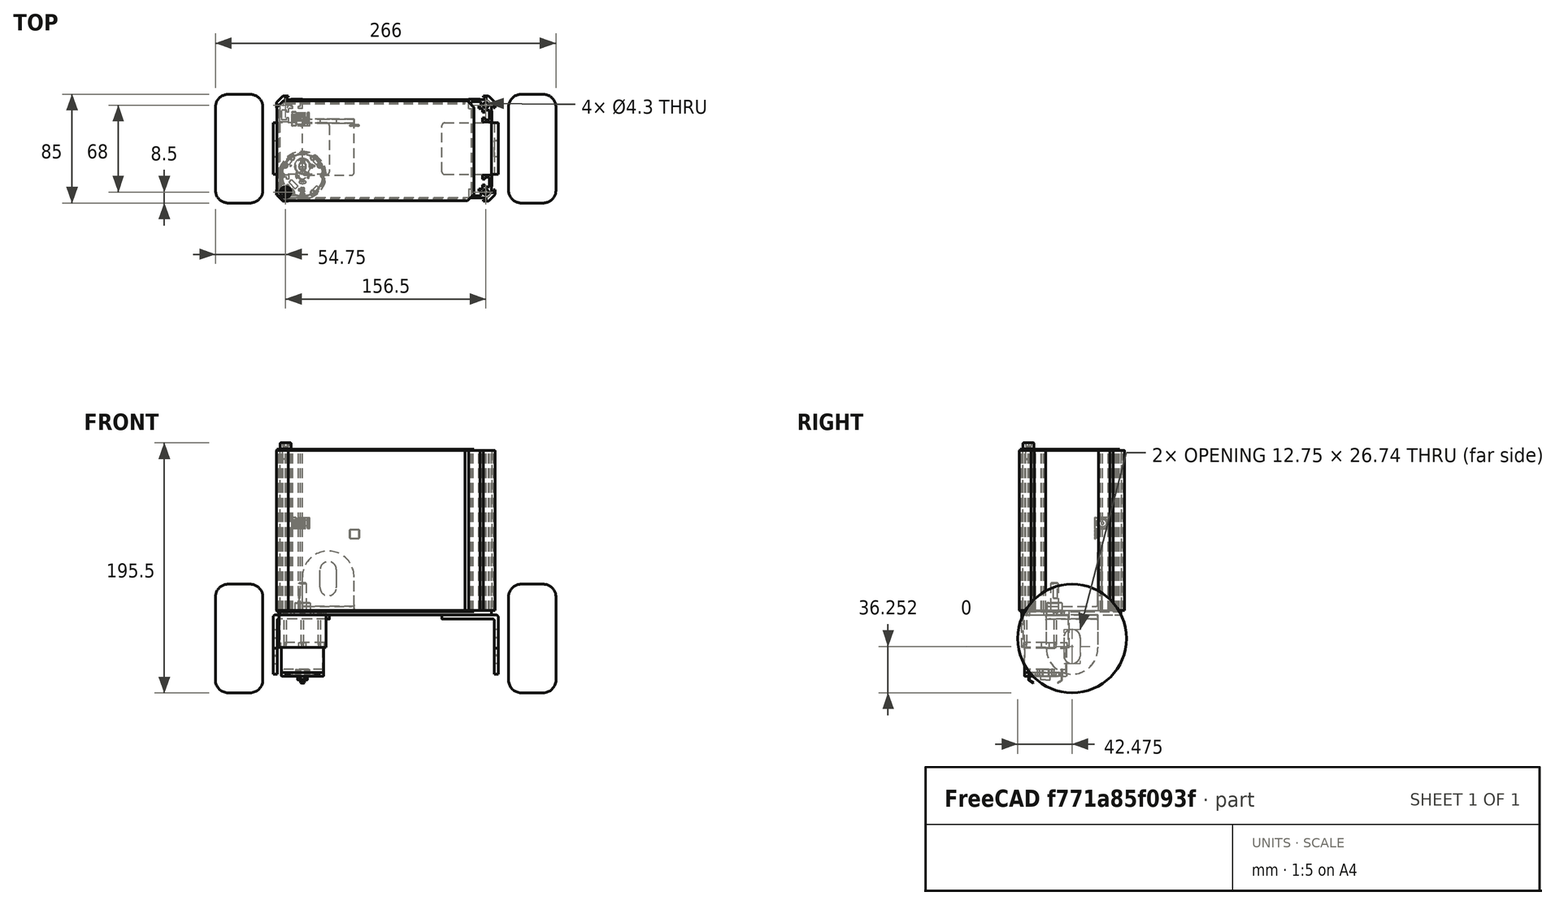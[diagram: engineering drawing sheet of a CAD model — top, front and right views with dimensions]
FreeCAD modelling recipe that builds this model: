
FCSTD DOCUMENT  (FreeCAD 0.18R16146 (Git))
Label: b1m1
License: All rights reserved
LicenseURL: http://en.wikipedia.org/wiki/All_rights_reserved
objects: Part::Feature×76, Part::Box×10, Part::Cylinder×5, App::DocumentObjectGroup×4, Part::Fillet×4, App::Part×3, Part::Cut×3, Part::Chamfer×2, Part::MultiFuse×2, Part::FeaturePython×1
note: 103 computed .brp shape members not serialized (recipe doc carries the construction recipe); baked Part::Feature solids carry a one-line shape summary decoded from their .brp

FEATURE [Part::Feature] Fillet001  label="frame_001"
  Placement = pos=(0,0,0) rot=(0,0,1;3.14159rad)
  shape: bbox 20.35 x 20.35 x 125 mm, 40 faces (baked)
FEATURE [Part::Feature] Fillet002  label="frame_002"
  Placement = pos=(130,0,0) rot=(0,0,-1;1.5708rad)
  shape: bbox 20.35 x 20.35 x 125 mm, 40 faces (baked)
FEATURE [Part::Feature] Fillet003  label="frame_003"
  Placement = pos=(0,41.5,0) rot=(0,0,1;1.5708rad)
  shape: bbox 20.35 x 20.35 x 125 mm, 40 faces (baked)
FEATURE [Part::Feature] Fillet004  label="frame_004"
  Placement = pos=(130,41.5,0) rot=(0,0,1;0rad)
  shape: bbox 20.35 x 20.35 x 125 mm, 40 faces (baked)
FEATURE [Part::Feature] Part__Feature013001  label="power jack back-002"
  shape: bbox 2 x 10.5 x 8 mm, 39 faces (baked)
FEATURE [Part::Feature] Part__Feature005001  label="10 pins-013"
  shape: bbox 0.5 x 3 x 0.5 mm, 29 faces, 0 solids (baked)
FEATURE [Part::Feature] Part__Feature027001  label="8 pin-026"
  shape: bbox 0.5 x 3 x 0.5 mm, 13 faces, 0 solids (baked)
FEATURE [Part::Feature] Part__Feature048  label="PCB"
  shape: bbox 68 x 2 x 53 mm, 960 faces, 0 solids (baked)
FEATURE [Part::Feature] Part__Feature009001  label="10 pins-018"
  shape: bbox 0.5 x 3 x 0.5 mm, 29 faces, 0 solids (baked)
FEATURE [Part::Feature] Part__Feature002001  label="10 pins-017"
  shape: bbox 0.5 x 3 x 0.5 mm, 29 faces, 0 solids (baked)
FEATURE [Part::Feature] Part__Feature021001  label="8 pin-021"
  shape: bbox 21 x 8.5 x 2.5 mm, 78 faces, 0 solids (baked)
FEATURE [Part::Feature] Part__Feature007001  label="10 pins-014"
  shape: bbox 0.5 x 3 x 0.5 mm, 29 faces, 0 solids (baked)
FEATURE [Part::Feature] Part__Feature039001  label="6 pin-012"
  shape: bbox 16 x 8.5 x 2.5 mm, 69 faces, 0 solids (baked)
FEATURE [Part::Feature] Part__Feature012001  label="power jack-002"
  shape: bbox 12 x 11 x 9 mm, 137 faces (baked)
FEATURE [Part::Feature] Part__Feature023001  label="8 pin-025"
  shape: bbox 0.5 x 3 x 0.5 mm, 13 faces, 0 solids (baked)
FEATURE [Part::Feature] Part__Feature037001  label="8 pin-018"
  shape: bbox 0.5 x 3 x 0.5 mm, 13 faces, 0 solids (baked)
FEATURE [Part::Feature] Part__Feature038001  label="8 pin-022"
  shape: bbox 0.5 x 3 x 0.5 mm, 13 faces, 0 solids (baked)
FEATURE [Part::Feature] Part__Feature018001  label="pin 2-008"
  shape: bbox 5 x 10 x 2 mm, 34 faces, 0 solids (baked)
FEATURE [Part::Feature] Part__Feature031001  label="8 pin-027"
  shape: bbox 0.5 x 3 x 0.5 mm, 13 faces, 0 solids (baked)
FEATURE [Part::Feature] Part__Feature014001  label="power jack pin-002"
  shape: bbox 12.6 x 11.32 x 4 mm, 660 faces, 0 solids (baked)
FEATURE [Part::Feature] Part__Feature045001  label="6 pin-010"
  shape: bbox 0.5 x 3 x 0.5 mm, 13 faces, 0 solids (baked)
FEATURE [Part::Feature] Part__Feature032001  label="8 pin-029"
  shape: bbox 0.5 x 3 x 0.5 mm, 13 faces, 0 solids (baked)
FEATURE [Part::Feature] Part__Feature010001  label="10 pins-021"
  shape: bbox 0.5 x 3 x 0.5 mm, 29 faces, 0 solids (baked)
FEATURE [Part::Feature] Part__Feature026001  label="8 pin-032"
  shape: bbox 0.5 x 3 x 0.5 mm, 13 faces, 0 solids (baked)
FEATURE [Part::Feature] Part__Feature040001  label="6 pin-014"
  shape: bbox 0.5 x 3 x 0.5 mm, 13 faces, 0 solids (baked)
FEATURE [Part::Feature] Part__Feature008001  label="10 pins-020"
  shape: bbox 0.5 x 3 x 0.5 mm, 29 faces, 0 solids (baked)
FEATURE [Part::Feature] Part__Feature020001  label="chip-002"
  shape: bbox 7.6 x 1 x 7.6 mm, 182 faces (baked)
FEATURE [Part::Feature] Part__Feature004001  label="10 pins-012"
  shape: bbox 0.5 x 3 x 0.5 mm, 29 faces, 0 solids (baked)
FEATURE [Part::Feature] Part__Feature001001  label="10 pins-019"
  shape: bbox 26 x 8.5 x 2.5 mm, 96 faces, 0 solids (baked)
FEATURE [Part::Feature] Part__Feature036001  label="8 pin-023"
  shape: bbox 0.5 x 3 x 0.5 mm, 13 faces, 0 solids (baked)
FEATURE [Part::Feature] Part__Feature022001  label="8 pin-034"
  shape: bbox 0.5 x 3 x 0.5 mm, 13 faces, 0 solids (baked)
FEATURE [Part::Feature] Part__Feature043001  label="6 pin-015"
  shape: bbox 0.5 x 3 x 0.5 mm, 13 faces, 0 solids (baked)
FEATURE [Part::Feature] Part__Feature042001  label="6 pin-013"
  shape: bbox 0.5 x 3 x 0.5 mm, 13 faces, 0 solids (baked)
FEATURE [Part::Feature] Part__Feature028001  label="8 pin-024"
  shape: bbox 0.5 x 3 x 0.5 mm, 13 faces, 0 solids (baked)
FEATURE [Part::Feature] Part__Feature044001  label="6 pin-016"
  shape: bbox 0.5 x 3 x 0.5 mm, 13 faces, 0 solids (baked)
FEATURE [Part::Feature] Part__Feature006001  label="10 pins-015"
  shape: bbox 0.5 x 3 x 0.5 mm, 29 faces, 0 solids (baked)
FEATURE [Part::Feature] Part__Feature015001  label="power jack pin 1-002"
  shape: bbox 8.476 x 8 x 6.5 mm, 49 faces, 0 solids (baked)
FEATURE [Part::Feature] Part__Feature029001  label="8 pin-033"
  shape: bbox 0.5 x 3 x 0.5 mm, 13 faces, 0 solids (baked)
FEATURE [Part::Feature] Part__Feature017001  label="pin 2-006"
  shape: bbox 5 x 10 x 2 mm, 34 faces, 0 solids (baked)
FEATURE [Part::Feature] Part__Feature034001  label="8 pin-030"
  shape: bbox 0.5 x 3 x 0.5 mm, 13 faces, 0 solids (baked)
FEATURE [Part::Feature] Part__Feature041001  label="6 pin-011"
  shape: bbox 0.5 x 3 x 0.5 mm, 13 faces, 0 solids (baked)
FEATURE [Part::Feature] Part__Feature030001  label="8 pin-035"
  shape: bbox 21 x 8.5 x 2.5 mm, 78 faces, 0 solids (baked)
FEATURE [Part::Feature] Part__Feature025001  label="8 pin-019"
  shape: bbox 0.5 x 3 x 0.5 mm, 13 faces, 0 solids (baked)
FEATURE [Part::Feature] Part__Feature024001  label="8 pin-031"
  shape: bbox 0.5 x 3 x 0.5 mm, 13 faces, 0 solids (baked)
FEATURE [Part::Feature] Part__Feature047001  label="micro usb-002"
  shape: bbox 5.5 x 2.6 x 7.6 mm, 414 faces, 0 solids (baked)
FEATURE [Part::Feature] Part__Feature011001  label="10 pins-022"
  shape: bbox 0.5 x 3 x 0.5 mm, 29 faces, 0 solids (baked)
FEATURE [Part::Feature] Part__Feature035001  label="8 pin-028"
  shape: bbox 0.5 x 3 x 0.5 mm, 13 faces, 0 solids (baked)
FEATURE [Part::Feature] Part__Feature016001  label="button-002"
  shape: bbox 10.5 x 3 x 6.5 mm, 333 faces, 0 solids (baked)
FEATURE [Part::Feature] Part__Feature046001  label="6 pin-009"
  shape: bbox 0.5 x 3 x 0.5 mm, 13 faces, 0 solids (baked)
FEATURE [Part::Feature] Part__Feature019001  label="pin 2-007"
  shape: bbox 5 x 10 x 2 mm, 34 faces, 0 solids (baked)
FEATURE [Part::Feature] Part__Feature003001  label="10 pins-016"
  shape: bbox 0.5 x 3 x 0.5 mm, 29 faces, 0 solids (baked)
FEATURE [Part::Feature] Part__Feature033001  label="8 pin-020"
  shape: bbox 0.5 x 3 x 0.5 mm, 13 faces, 0 solids (baked)
FEATURE [App::Part] Part001  label="Arduino"
  Group = -> [Part__Feature048,Part__Feature009001,Part__Feature027001,Part__Feature002001,Part__Feature021001,Part__Feature007001,Part__Feature039001,Part__Feature012001,Part__Feature023001,Part__Feature037001,Part__Feature038001,Part__Feature018001,Part__Feature031001,Part__Feature014001,Part__Feature045001,Part__Feature032001,Part__Feature010001,Part__Feature026001,Part__Feature040001,Part__Feature008001,+28 more]
  License = CC BY 3.0
  LicenseURL = http://creativecommons.org/licenses/by/3.0/
  Origin = -> Origin001
  Placement = pos=(106.5,49,34.5) rot=(0.57735,-0.57735,-0.57735;2.0944rad)
FEATURE [Part::FeaturePython] Screw  label="M5x8-Screw"  # Fasteners workbench fastener (typed FeaturePython)
  Placement = pos=(-13.25,-13.25,126) rot=(0,0,1;0rad)
  diameter = 6
  invert = false
  length = 0
  matchOuter = false
  offset = 0
  thread = false
  type = 15
FEATURE [Part::Feature] Part__Feature  label="GEARED BODY, MOTOR, JGB37-520"
  shape: bbox 37 x 37 x 29.02 mm, 71 faces (baked)
FEATURE [Part::Feature] Part__Feature047002  label="DC MOTOR, JGB37-520"
  Placement = pos=(0,0,-29) rot=(0,0,1;3.14159rad)
  shape: bbox 35.72 x 35.72 x 19.5 mm, 11 faces (baked)
FEATURE [Part::Feature] Part__Feature047003  label="MOTOR SHAFT, JGB37-520"
  Placement = pos=(0,7,0) rot=(0,0,1;2.80085rad)
  shape: bbox 6.001 x 6.001 x 21.5 mm, 8 faces (baked)
FEATURE [Part::Feature] Part__Feature047004  label="SHAFT COUPLER, JGB37-520"
  Placement = pos=(0,7,0) rot=(0,0,1;0.886941rad)
  shape: bbox 12 x 12 x 6 mm, 8 faces (baked)
FEATURE [Part::Feature] Part__Feature047005  label="COUPLING BRACKET, GEARED BODY TO DC MOTOR, JGB37-520"
  Placement = pos=(0,0,-25) rot=(0,0,1;0rad)
  shape: bbox 34 x 34 x 4 mm, 18 faces (baked)
FEATURE [Part::Feature] Part__Feature047006  label="PLASTIC COVER, DC MOTOR, JGB37-520"
  Placement = pos=(0,2e-15,-48.5) rot=(0,0,1;0rad)
  shape: bbox 35.72 x 35.72 x 8.501 mm, 90 faces (baked)
FEATURE [Part::Feature] Part__Feature047007  label="CONNECTION, DC MOTOR, JGB37-520"
  Placement = pos=(0,12.8,-50.25) rot=(0,1,0;3.14159rad)
  shape: bbox 3 x 3.971 x 10.88 mm, 21 faces (baked)
FEATURE [Part::Feature] Part__Feature047008  label="CONNECTION, DC MOTOR, JGB37-521"
  Placement = pos=(8.9e-14,-12.8,-50.25) rot=(1,0,0;3.14159rad)
  shape: bbox 3 x 3.971 x 10.88 mm, 21 faces (baked)
FEATURE [Part::Feature] Part__Feature047009  label="pan cross head_am_B18.6.7M - M2 x 0.4 x 25 Type I Cross Recessed PHMS --25N"
  Placement = pos=(-13.4234,7.75,-2e-15) rot=(0.706503,-0.041307,-0.706503;3.22416rad)
  shape: bbox 4.3 x 4.3 x 26.6 mm, 23 faces (baked)
FEATURE [Part::Feature] Part__Feature047010  label="pan cross head_am_B18.6.7M - M2 x 0.4 x 25 Type I Cross Recessed PHMS --25N001"
  Placement = pos=(-4e-15,-15.5,-2e-15) rot=(0.481713,0.732055,-0.481713;1.87776rad)
  shape: bbox 4.316 x 4.705 x 26.6 mm, 23 faces (baked)
FEATURE [Part::Feature] Part__Feature047011  label="pan cross head_am_B18.6.7M - M2 x 0.4 x 25 Type I Cross Recessed PHMS --25N002"
  Placement = pos=(13.4234,7.75,-2e-15) rot=(-0.409303,0.81544,0.409303;1.77342rad)
  shape: bbox 4.727 x 4.88 x 26.6 mm, 23 faces (baked)
FEATURE [App::Part] JGB37_520  label="JGB37-520_001"
  Group = -> [Part__Feature,Part__Feature047002,Part__Feature047003,Part__Feature047004,Part__Feature047005,Part__Feature047006,Part__Feature047007,Part__Feature047008,Part__Feature047009,Part__Feature047010,Part__Feature047011]
  Origin = -> Origin
  Placement = pos=(-20,20.75,-29) rot=(-0.57735,0.57735,0.57735;4.18879rad)
FEATURE [Part::Feature] Part__Feature047012  label="DC MOTOR, JGB37-521"
  Placement = pos=(0,0,-29) rot=(0,0,1;3.14159rad)
  shape: bbox 35.72 x 35.72 x 19.5 mm, 11 faces (baked)
FEATURE [Part::Feature] Part__Feature047013  label="CONNECTION, DC MOTOR, JGB37-522"
  Placement = pos=(0,12.8,-50.25) rot=(0,1,0;3.14159rad)
  shape: bbox 3 x 3.971 x 10.88 mm, 21 faces (baked)
FEATURE [Part::Feature] Part__Feature047014  label="pan cross head_am_B18.6.7M - M2 x 0.4 x 25 Type I Cross Recessed PHMS --25N003"
  Placement = pos=(-13.4234,7.75,-2e-15) rot=(0.706503,-0.041307,-0.706503;3.22416rad)
  shape: bbox 4.3 x 4.3 x 26.6 mm, 23 faces (baked)
FEATURE [Part::Feature] Part__Feature047015  label="MOTOR SHAFT, JGB37-521"
  Placement = pos=(0,7,0) rot=(0,0,1;2.80085rad)
  shape: bbox 6.001 x 6.001 x 21.5 mm, 8 faces (baked)
FEATURE [Part::Feature] Part__Feature047016  label="CONNECTION, DC MOTOR, JGB37-523"
  Placement = pos=(8.9e-14,-12.8,-50.25) rot=(1,0,0;3.14159rad)
  shape: bbox 3 x 3.971 x 10.88 mm, 21 faces (baked)
FEATURE [Part::Feature] Part__Feature047017  label="COUPLING BRACKET, GEARED BODY TO DC MOTOR, JGB37-521"
  Placement = pos=(0,0,-25) rot=(0,0,1;0rad)
  shape: bbox 34 x 34 x 4 mm, 18 faces (baked)
FEATURE [Part::Feature] Part__Feature047018  label="pan cross head_am_B18.6.7M - M2 x 0.4 x 25 Type I Cross Recessed PHMS --25N004"
  Placement = pos=(-4e-15,-15.5,-2e-15) rot=(0.481713,0.732055,-0.481713;1.87776rad)
  shape: bbox 4.316 x 4.705 x 26.6 mm, 23 faces (baked)
FEATURE [Part::Feature] Part__Feature047019  label="SHAFT COUPLER, JGB37-521"
  Placement = pos=(0,7,0) rot=(0,0,1;0.886941rad)
  shape: bbox 12 x 12 x 6 mm, 8 faces (baked)
FEATURE [Part::Feature] Part__Feature047020  label="PLASTIC COVER, DC MOTOR, JGB37-521"
  Placement = pos=(0,2e-15,-48.5) rot=(0,0,1;0rad)
  shape: bbox 35.72 x 35.72 x 8.501 mm, 90 faces (baked)
FEATURE [Part::Feature] Part__Feature047021  label="pan cross head_am_B18.6.7M - M2 x 0.4 x 25 Type I Cross Recessed PHMS --25N005"
  Placement = pos=(13.4234,7.75,-2e-15) rot=(-0.409303,0.81544,0.409303;1.77342rad)
  shape: bbox 4.727 x 4.88 x 26.6 mm, 23 faces (baked)
FEATURE [Part::Feature] Part__Feature047022  label="GEARED BODY, MOTOR, JGB37-521"
  shape: bbox 37 x 37 x 29.02 mm, 71 faces (baked)
FEATURE [App::Part] JGB37_521  label="JGB37-520_002"
  Group = -> [Part__Feature047022,Part__Feature047012,Part__Feature047015,Part__Feature047019,Part__Feature047017,Part__Feature047020,Part__Feature047013,Part__Feature047016,Part__Feature047014,Part__Feature047018,Part__Feature047021]
  Origin = -> Origin002
  Placement = pos=(150,20.75,-29) rot=(0.57735,0.57735,0.57735;2.0944rad)
FEATURE [App::DocumentObjectGroup] Group001  label="Eletronics"
  Group = -> [Part001,JGB37_520,JGB37_521]
FEATURE [Part::Box] Box  label="Cube"
  AttacherType = Attacher::AttachEngine3D
  Height = 1
  Length = 154
  Placement = pos=(-20,-20,-1) rot=(0,0,1;0rad)
  Width = 78
FEATURE [Part::Chamfer] Chamfer  label="Cover_botton"
  Base = -> Box
  Edges = 4 edges r=5: [Edge1,Edge3,Edge5,Edge7]
FEATURE [App::DocumentObjectGroup] Group002  label="Frame"
  Group = -> [Fillet001,Fillet002,Fillet003,Fillet004]
FEATURE [Part::Box] Box001  label="Cube001"
  AttacherType = Attacher::AttachEngine3D
  Height = 1
  Length = 154
  Placement = pos=(-20,-20,-1) rot=(0,0,1;0rad)
  Width = 78
FEATURE [Part::Chamfer] Chamfer001  label="Cover_top"
  Base = -> Box001
  Edges = 4 edges r=5: [Edge1,Edge3,Edge5,Edge7]
  Placement = pos=(0,0,126) rot=(0,0,1;0rad)
FEATURE [Part::Box] Box002  label="Cover_front"
  AttacherType = Attacher::AttachEngine3D
  Height = 125
  Length = 140
  Placement = pos=(-13,-19,0) rot=(0,0,1;0rad)
  Width = 1
FEATURE [Part::Box] Box003  label="Cover_back"
  AttacherType = Attacher::AttachEngine3D
  Height = 125
  Length = 140
  Placement = pos=(-13,56,0) rot=(0,0,1;0rad)
  Width = 1
FEATURE [Part::Box] Box004  label="Cover_back001"
  AttacherType = Attacher::AttachEngine3D
  Height = 125
  Length = 1
  Placement = pos=(-19,-13,0) rot=(0,0,1;0rad)
  Width = 64
FEATURE [Part::Box] Box005  label="Cover_back002"
  AttacherType = Attacher::AttachEngine3D
  Height = 125
  Length = 1
  Placement = pos=(132,-13,0) rot=(0,0,1;0rad)
  Width = 64
FEATURE [App::DocumentObjectGroup] Group003  label="Cover"
  Group = -> [Chamfer,Chamfer001,Box002,Box003,Box004,Box005]
FEATURE [Part::Cylinder] Cylinder
  Angle = 360
  AttacherType = Attacher::AttachEngine3D
  Height = 37
  Placement = pos=(-60,20.75,14) rot=(0,1,0;1.5708rad)
  Radius = 42.5
FEATURE [Part::Cylinder] Cylinder001
  Angle = 360
  AttacherType = Attacher::AttachEngine3D
  Height = 37
  Placement = pos=(153,20.75,14) rot=(0,1,0;1.5708rad)
  Radius = 42.5
FEATURE [Part::Box] Box006  label="Cube002"
  AttacherType = Attacher::AttachEngine3D
  Height = 3.5
  Length = 165
  Placement = pos=(0,0,-60) rot=(0,0,1;0rad)
  Width = 76.5
FEATURE [Part::Fillet] Fillet
  Base = -> Box006
  Edges = 4 edges r=5: [Edge1,Edge3,Edge5,Edge7]
  Placement = pos=(-17.5,-17.5,56.5) rot=(0,0,1;0rad)
FEATURE [App::DocumentObjectGroup] Group  label="Mechanics"
  Group = -> [Screw,Box,Group002,Group003,Fillet]
FEATURE [Part::Fillet] Fillet005
  Base = -> Cylinder001
  Edges = 2 edges r=10: [Edge1,Edge3]
  Placement = pos=(8,0,-36) rot=(0,0,1;0rad)
FEATURE [Part::Fillet] Fillet006
  Base = -> Cylinder
  Edges = 2 edges r=10: [Edge1,Edge3]
  Placement = pos=(-8,0,-36) rot=(0,0,1;0rad)
FEATURE [Part::Cylinder] Cylinder002
  Angle = 360
  AttacherType = Attacher::AttachEngine3D
  Height = 3.25
  Placement = pos=(20.12,44,31.75) rot=(1,0,0;1.5708rad)
  Radius = 6.375
FEATURE [Part::Box] Box007  label="Cube003"
  AttacherType = Attacher::AttachEngine3D
  Height = 3.25
  Length = 40.25
  Width = 44
FEATURE [Part::Box] Box008  label="Cube004"
  AttacherType = Attacher::AttachEngine3D
  Height = 14
  Length = 12.75
  Placement = pos=(13.75,40.75,18) rot=(0,0,1;0rad)
  Width = 3.25
FEATURE [Part::Cylinder] Cylinder003
  Angle = 360
  AttacherType = Attacher::AttachEngine3D
  Height = 3.25
  Placement = pos=(20.12,44,26.25) rot=(1,0,0;1.5708rad)
  Radius = 20.12
FEATURE [Part::Cylinder] Cylinder004
  Angle = 360
  AttacherType = Attacher::AttachEngine3D
  Height = 3.25
  Placement = pos=(20.12,44,17.75) rot=(1,0,0;1.5708rad)
  Radius = 6.375
FEATURE [Part::Box] Box009  label="Cube005"
  AttacherType = Attacher::AttachEngine3D
  Height = 26
  Length = 40.25
  Placement = pos=(0,40.75,0) rot=(0,0,1;0rad)
  Width = 3.25
FEATURE [Part::MultiFuse] Fusion
  Shapes = -> [Box007,Box009]
FEATURE [Part::MultiFuse] Fusion001
  Shapes = -> [Cylinder003,Fusion]
FEATURE [Part::Cut] Cut
  Base = -> Fusion001
  Tool = -> Cylinder002
FEATURE [Part::Cut] Cut001
  Base = -> Cut
  Tool = -> Cylinder004
FEATURE [Part::Cut] Cut002
  Base = -> Cut001
  Tool = -> Box008
FEATURE [Part::Feature] Fillet007  label="Motor_support_001"
  Placement = pos=(21,40.85,-3.5) rot=(0.707107,-0.707107,0;3.14159rad)
  shape: bbox 44 x 40.25 x 46.37 mm, 20 faces (baked)
FEATURE [Part::Fillet] Fillet008
  Base = -> Cut002
  Edges = 4 edges: [Edge46 r=1,Edge53 r=2,Edge65 r=2,Edge67 r=2]
FEATURE [Part::Feature] Fillet009  label="Motor_support_002"
  Placement = pos=(109,0.6,-3.5) rot=(0.707107,0.707107,0;3.14159rad)
  shape: bbox 44 x 40.25 x 46.37 mm, 20 faces (baked)
